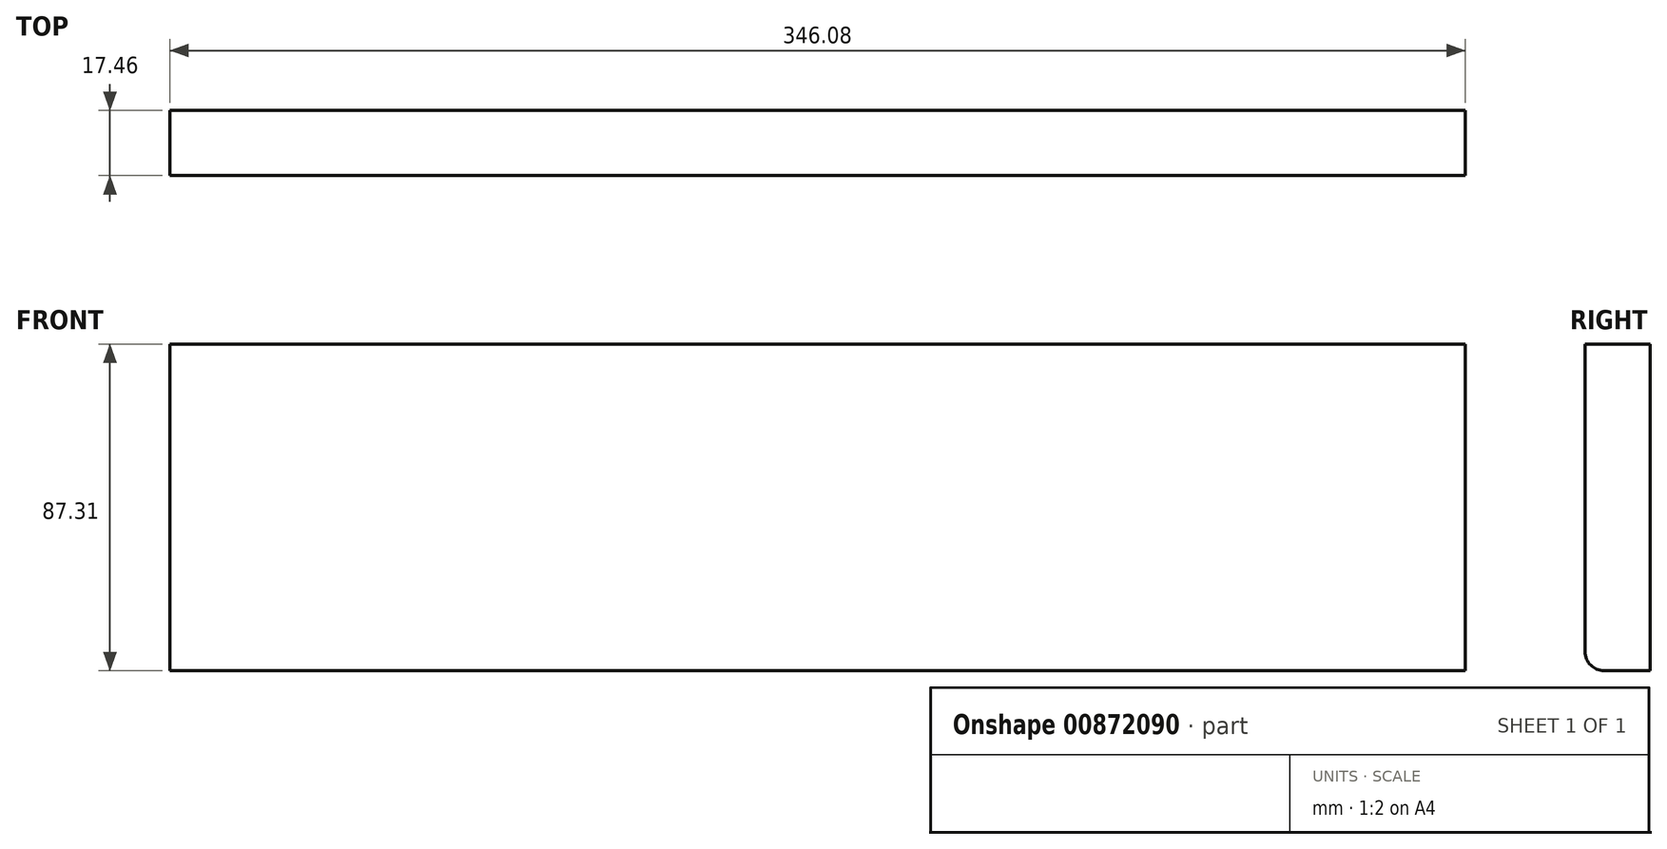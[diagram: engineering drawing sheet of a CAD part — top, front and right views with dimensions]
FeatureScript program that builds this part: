
annotation { "Feature Type Name" : "Feature", "Feature Type Description" : "" }
export const myFeature = defineFeature(function(context is Context, id is Id, definition is map)
    precondition{}
    {
        {
            var Q0;
            Q0=qCreatedBy(makeId("Front.planeOp"),FACE);
            var sketch = newSketch(context, id + "F0", { "sketchPlane" : qUnion([Q0])});
            skLineSegment(sketch, "E0.bottom", {"start": v(0, 0) * mm, "end": v(346.08, 0) * mm});
            skLineSegment(sketch, "E0.top", {"start": v(0, 87.31) * mm, "end": v(346.08, 87.31) * mm});
            skLineSegment(sketch, "E0.left", {"start": v(0, 0) * mm, "end": v(0, 87.31) * mm});
            skLineSegment(sketch, "E0.right", {"start": v(346.08, 0) * mm, "end": v(346.08, 87.31) * mm});
            skSolve(sketch);
        }
        {
            var Q0;
            Q0=qSketchRegion(id+"F0",true);
            extrude(context, id + "F1", {"entities" : qUnion([Q0]), "depth" : 17.46 * mm});
        }
        {
            var Q0;
            Q0=makeQuery(id+"F1.opExtrude","CAP_EDGE",EDGE,{"disambiguationData":[OSD([sQuery(id+"F0.wireOp",EDGE,"E0.bottom")])],"isStart":false});
            fillet(context, id + "F2", {"entities" : qUnion([Q0]), "radius" : 5.08 * mm, "tangentPropagation" : true, "allowEdgeOverflow" : false});
        }
    });
